# Revit family: Haworth_JiveTable_RoundLegs
name_source: partatom
category: Furniture Systems
revit_build: Autodesk Revit 2018 (Build: 20170223_1515(x64)
units: mm (PartAtom-declared; Revit-internal decimal feet)

## family parameters
Always vertical = Yes
Cut with Voids When Loaded = No
OmniClass Number = 23.40.70.14.64.21
OmniClass Title = Systems Furniture
Part Type = Normal
Room Calculation Point = No
Round Connector Dimension = Use Diameter
Shared = No
Work Plane-Based = No

## types (22) — shared parameters
Assembly Code = E2020200
Custom Size = No
Manufacturer = Haworth, Inc.
Max. Depth Width = 30"
Max. Height = 29"
Min. Depth Width = 12"
Min. Height = 16"
Model = Hawoth Jive
Revision Number = 0
Size = Verify Final Dim. w/ Haworth
Standard Depths Widths = 24, 30, 36, 42, 48, 54, 60 in.
Standard Height = 16, 20, 29
Table Thickness = 1 3/16"
URL = https://www.haworth.com
URL - Product = https://www.haworth.com
Warranty = http://www.haworth.com

## per-type parameters (varying)
| type | Actual Casters | Actual Depth | Actual Glides | Actual Height | Casters | DW | Depth | Description | Glides | Height | Leg Distance | Leg Height | Post Extruded Leg | Post Leg Spacing | Post Round Leg |
| 24d 24w 16h - Post Extruded Base - With Glides | No | 12" | Yes | 16" | No | 12" | 24" | Haworth Jive Table Round Legs - 24d 24w 16h - Post Extruded Base - With Glides | Yes | 16" | 6" | 14 13/16" | Yes | 3 127/128" | No |
| 30d 30w 16h - Post Extruded Base - With Glides | No | 15" | Yes | 16" | No | 15" | 30" | Haworth Jive Table Round Legs - 30d 30w 16h - Post Extruded Base - With Glides | Yes | 16" | 8" | 14 13/16" | Yes | 6 127/128" | No |
| 36d 36w 16h - Post Extruded Base - With Glides | No | 18" | Yes | 16" | No | 18" | 36" | Haworth Jive Table Round Legs - 36d 36w 16h - Post Extruded Base - With Glides | Yes | 16" | 10" | 14 13/16" | Yes | 9 127/128" | No |
| 42d 42w 16h - Post Extruded Base - With Glides | No | 21" | Yes | 16" | No | 21" | 42" | Haworth Jive Table Round Legs - 42d 42w 16h - Post Extruded Base - With Glides | Yes | 16" | 12" | 14 13/16" | Yes | 12 127/128" | No |
| 48d 48w 16h - Post Extruded Base - With Glides | No | 24" | Yes | 16" | No | 24" | 48" | Haworth Jive Table Round Legs - 48d 48w 16h - Post Extruded Base - With Glides | Yes | 16" | 13" | 14 13/16" | Yes | 15 127/128" | No |
| 24d 24d 20h - Post Extruded Base - With Glides | No | 12" | Yes | 20" | No | 12" | 24" | Haworth Jive Table Round Legs - 24d 24d 20h - Post Extruded Base - With Glides | Yes | 20" | 6" | 18 13/16" | Yes | 3 127/128" | No |
| 30d 30w 20h - Post Extruded Base - With Glides | No | 15" | Yes | 20" | No | 15" | 30" | Haworth Jive Table Round Legs - 30d 30w 20h - Post Extruded Base - With Glides | Yes | 20" | 8" | 18 13/16" | Yes | 6 127/128" | No |
| 36d 36w 20h - Post Extruded Base - With Glides | No | 18" | Yes | 20" | No | 18" | 36" | Haworth Jive Table Round Legs - 36d 36w 20h - Post Extruded Base - With Glides | Yes | 20" | 10" | 18 13/16" | Yes | 9 127/128" | No |
| 42d 42w 20h - Post Extruded Base - With Glides | No | 21" | Yes | 20" | No | 21" | 42" | Haworth Jive Table Round Legs - 42d 42w 20h - Post Extruded Base - With Glides | Yes | 20" | 12" | 18 13/16" | Yes | 12 127/128" | No |
| 48d 48w 20h - Post Extruded Base - With Glides | No | 24" | Yes | 20" | No | 24" | 48" | Haworth Jive Table Round Legs - 48d 48w 20h - Post Extruded Base - With Glides | Yes | 20" | 13" | 18 13/16" | Yes | 15 127/128" | No |
| 42d 42w 29h - Post Extruded Base - With Glides | No | 21" | Yes | 29" | No | 21" | 42" | Haworth Jive Table Round Legs - 42d 42w 29h - Post Extruded Base - With Glides | Yes | 29" | 12" | 27 13/16" | Yes | 12 127/128" | No |
| 48d 48w 29h - Post Extruded Base - With Glides | No | 24" | Yes | 29" | No | 24" | 48" | Haworth Jive Table Round Legs - 48d 48w 29h - Post Extruded Base - With Glides | Yes | 29" | 13" | 27 13/16" | Yes | 15 127/128" | No |
| 54d 54w 29h - Post Extruded Base - With Glides | No | 27" | Yes | 29" | No | 27" | 54" | Haworth Jive Table Round Legs - 54d 54w 29h - Post Extruded Base - With Glides | Yes | 29" | 15" | 27 13/16" | Yes | 18 127/128" | No |
| 60d 60w 29h - Post Extruded Base - With Glides | No | 30" | Yes | 29" | No | 30" | 60" | Haworth Jive Table Round Legs - 60d 60w 29h - Post Extruded Base - With Glides | Yes | 29" | 16" | 27 13/16" | Yes | 21 127/128" | No |
| 42d 42w 29h - Post Extruded Base - With Casters | Yes | 21" | No | 29" | Yes | 21" | 42" | Haworth Jive Table Round Legs - 42d 42w 29h - Post Extruded Base - With Casters | No | 29" | 12" | 27 13/16" | Yes | 12 127/128" | No |
| 48d 48w 29h - Post Extruded Base - With Casters | Yes | 24" | No | 29" | Yes | 24" | 48" | Haworth Jive Table Round Legs - 48d 48w 29h - Post Extruded Base - With Casters | No | 29" | 13" | 27 13/16" | Yes | 15 127/128" | No |
| 54d 54w 29h - Post Extruded Base - With Casters | Yes | 27" | No | 29" | Yes | 27" | 54" | Haworth Jive Table Round Legs - 54d 54w 29h - Post Extruded Base - With Casters | No | 29" | 15" | 27 13/16" | Yes | 18 127/128" | No |
| 60d 60w 29h - Post Extruded Base - With Casters | Yes | 30" | No | 29" | Yes | 30" | 60" | Haworth Jive Table Round Legs - 60d 60w 29h - Post Extruded Base - With Casters | No | 29" | 16" | 27 13/16" | Yes | 21 127/128" | No |
| 42d 42w 29h - Post Round Base - With Casters | Yes | 21" | No | 29" | Yes | 21" | 42" | Haworth Jive Table Round Legs - 42d 42w 29h - Post Round Base - With Casters | No | 29" | 12" | 27 13/16" | No | 12 127/128" | Yes |
| 48d 48w 29h - Post Round Base - With Casters | Yes | 24" | No | 29" | Yes | 24" | 48" | Haworth Jive Table Round Legs - 48d 48w 29h - Post Round Base - With Casters | No | 29" | 13" | 27 13/16" | No | 15 127/128" | Yes |
| 42d 42w 29h - Post Round Base - With Glides | No | 21" | Yes | 29" | No | 21" | 42" | Haworth Jive Table Round Legs - 42d 42w 29h - Post Round Base - With Glides | Yes | 29" | 12" | 27 13/16" | No | 12 127/128" | Yes |
| 48d 48w 29h - Post Round Base - With Glides | No | 24" | Yes | 29" | No | 24" | 48" | Haworth Jive Table Round Legs - 48d 48w 29h - Post Round Base - With Glides | Yes | 29" | 13" | 27 13/16" | No | 15 127/128" | Yes |

## geometry (parser evidence)
native form markers: Sweep x30
no freeform markers — native parametric forms only
